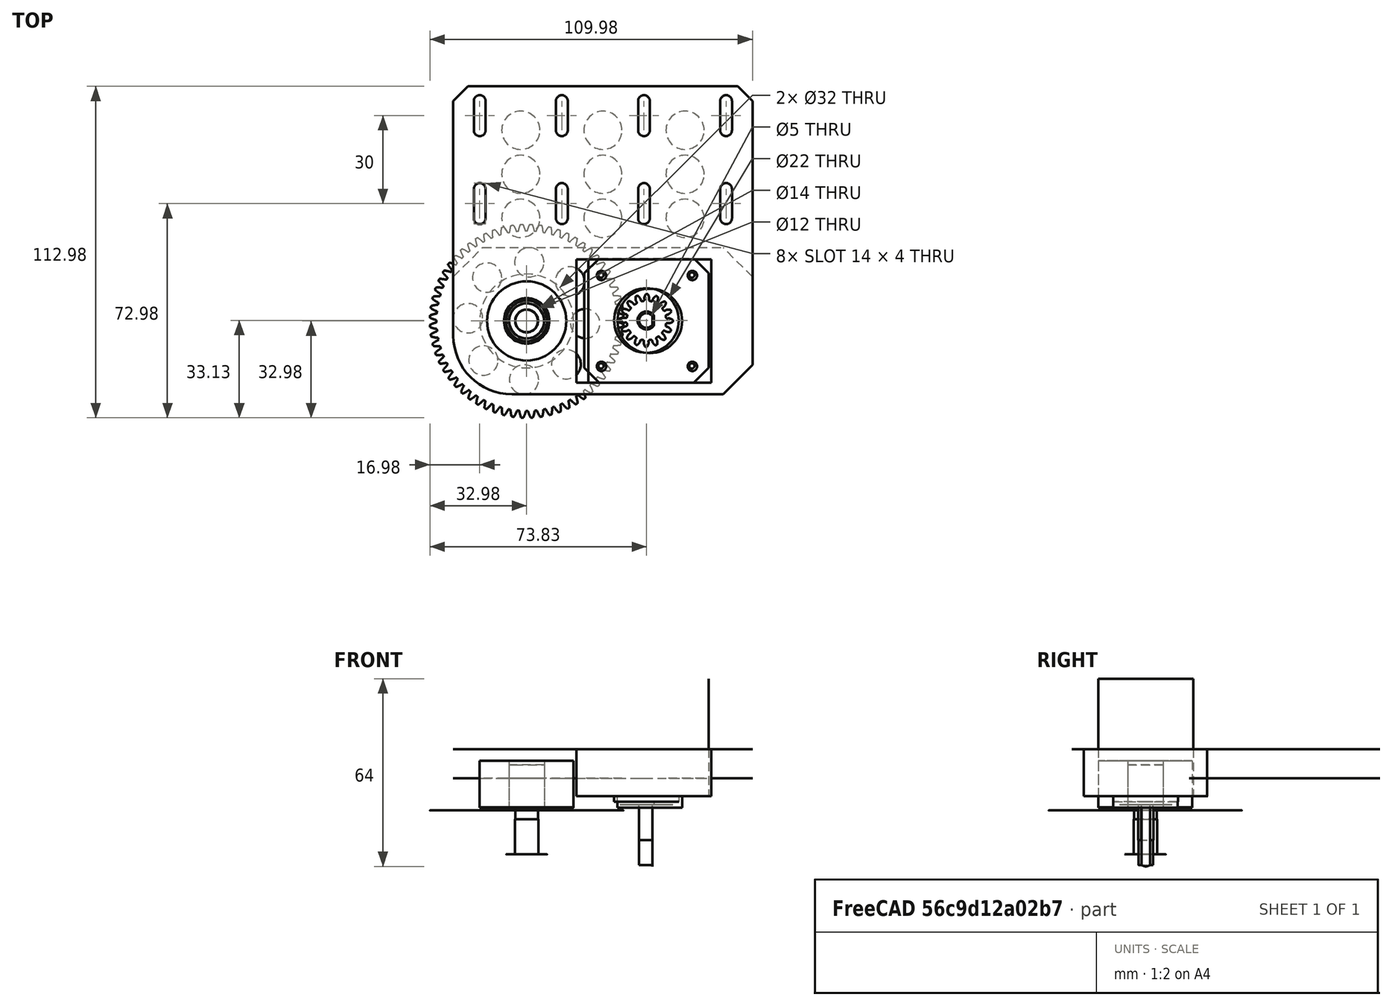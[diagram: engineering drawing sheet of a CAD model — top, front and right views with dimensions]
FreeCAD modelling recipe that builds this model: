
FCSTD DOCUMENT  (FreeCAD 2020.12.13R23076 +3015 (Git))
Label: przekladnia
License: All rights reserved
LicenseURL: http://en.wikipedia.org/wiki/All_rights_reserved
objects: Part::FeaturePython×44, App::FeaturePython×43, App::Link×7
note: 43 computed .brp shape members not serialized (recipe doc carries the construction recipe); baked Part::Feature solids carry a one-line shape summary decoded from their .brp
EXTERNAL_REF file=plytaprzekladni.FCStd obj=Body
EXTERNAL_REF file=krokowiec-nema17.FCStd obj=Body
EXTERNAL_REF file=kolkozebmodul1fi5przekl.FCStd obj=Body
EXTERNAL_REF file=lozysko 5201.FCStd obj=Body
EXTERNAL_REF file=koloprzekladni.FCStd obj=Body
EXTERNAL_REF file=m8x40imb.FCStd obj=Body
EXTERNAL_REF file=wkladkaloz.FCStd obj=Body

FEATURE [App::Link] Link001  label="plyta-przekadni"
  LinkPlacement = pos=(0,0,0) rot=(-1,0,0;3.14159rad)
  LinkedObject = -> <external plytaprzekladni.FCStd>#Body
  Placement = pos=(0,0,0) rot=(-1,0,0;3.14159rad)
  SyncGroupVisibility = false
  _LinkVersion = 1
FEATURE [App::Link] Link003  label="nema17"
  LinkPlacement = pos=(0.85,0.15,24) rot=(1,0,0;3.14159rad)
  LinkedObject = -> <external krokowiec-nema17.FCStd>#Body
  Placement = pos=(0.85,0.15,24) rot=(1,0,0;3.14159rad)
  SyncGroupVisibility = false
  _LinkVersion = 1
FEATURE [App::Link] Link  label="kolkozebstozniskie"
  LinkPlacement = pos=(0.85,0.15,-31) rot=(0,0,-1;0.012799rad)
  LinkedObject = -> <external kolkozebmodul1fi5przekl.FCStd>#Body
  Placement = pos=(0.85,0.15,-31) rot=(0,0,-1;0.012799rad)
  SyncGroupVisibility = false
  _LinkVersion = 1
FEATURE [App::Link] Link004  label="lozysko5201"
  LinkPlacement = pos=(-40,1.5e-15,-11.95) rot=(0,0,-1;0.034901rad)
  LinkedObject = -> <external lozysko 5201.FCStd>#Body
  Placement = pos=(-40,1.5e-15,-11.95) rot=(0,0,-1;0.034901rad)
  SyncGroupVisibility = false
  _LinkVersion = 1
FEATURE [App::Link] Link006  label="koloprzekladni"
  LinkPlacement = pos=(-40,3.8e-15,-30.9) rot=(-0.999741,0.022763,0;3.14159rad)
  LinkedObject = -> <external koloprzekladni.FCStd>#Body
  Placement = pos=(-40,3.8e-15,-30.9) rot=(-0.999741,0.022763,0;3.14159rad)
  SyncGroupVisibility = false
  _LinkVersion = 1
FEATURE [App::Link] Link007  label="m8x40imb"
  LinkPlacement = pos=(-40,5.4e-15,-43.9) rot=(0,0,-1;0.002436rad)
  LinkedObject = -> <external m8x40imb.FCStd>#Body
  Placement = pos=(-40,5.4e-15,-43.9) rot=(0,0,-1;0.002436rad)
  SyncGroupVisibility = false
  _LinkVersion = 1
FEATURE [App::Link] Link005  label="wkladkamimosr"
  LinkPlacement = pos=(-40,2.5e-15,-20.9) rot=(0,0,1;3.95082rad)
  LinkedObject = -> <external wkladkaloz.FCStd>#Body
  Placement = pos=(-40,2.5e-15,-20.9) rot=(0,0,1;3.95082rad)
  SyncGroupVisibility = false
  _LinkVersion = 1
FEATURE [Part::FeaturePython] Parts  # WARN: FeaturePython — macro-defined, semantics opaque (R4)
  Group = -> [Link001,Link003,Link,Link004,Link006,Link007,Link005]
  GroupMode = 0
  _LinkVersion = 1
FEATURE [Part::FeaturePython] Assembly  label="przekladnia"  # WARN: FeaturePython — macro-defined, semantics opaque (R4)
  AutoRelax = true
  BuildShape = 0
  Freeze = false
  Group = -> [Constraints,Elements,Parts]
  Verbose = false
  _LinkVersion = 1
  _SolverType = 1
  _Version = 1
FEATURE [App::FeaturePython] Constraints  # WARN: FeaturePython — macro-defined, semantics opaque (R4)
  Group = -> [Constraint,Constraint002,Constraint005,Constraint015,Constraint016,Constraint020,Constraint021,Constraint022,Constraint023,Constraint024,Constraint025,Constraint026,Constraint027,Constraint028]
  _LinkVersion = 1
  _Version = 1
FEATURE [App::FeaturePython] Elements  # WARN: FeaturePython — macro-defined, semantics opaque (R4)
  Group = -> [_Element,_Element001,_Element002,_Element003,_Element004,_Element006,_Element007,_Element009,_Element010,_Element011,_Element012,_Element014,_Element016,_Element017,_Element019,_Element022,_Element023,_Element024,_Element025,_Element028,Element,Element001,_Element029,_Element030,_Element031,_Element032,_Element033,_Element034,_Element035,_Element036,_Element037,_Element038,_Element039,_Element040,+8 more]
  _LinkVersion = 1
FEATURE [App::FeaturePython] Constraint  label="Locked"  # WARN: FeaturePython — macro-defined, semantics opaque (R4)
  Disabled = false
  Group = -> [ElementLink]
  _ConstraintType = 0
  _LinkVersion = 1
  _Parent = -> Constraints
FEATURE [App::FeaturePython] ElementLink  label="_Element"  # link proxy (typed FeaturePython)
  LinkTransform = true
  LinkedObject = -> _Element
  _LinkVersion = 1
  _Parent = -> Constraint
FEATURE [Part::FeaturePython] _Element  # link proxy (typed FeaturePython)
  Detach = false
  LinkTransform = true
  LinkedObject = -> Link001 [Pocket005.Face1]
  _LinkVersion = 1
  _Parent = -> Elements
FEATURE [Part::FeaturePython] _Element001  # link proxy (typed FeaturePython)
  Detach = false
  LinkTransform = true
  LinkedObject = -> Link001 [Pocket005.Face57]
  _LinkVersion = 1
  _Parent = -> Elements
FEATURE [Part::FeaturePython] _Element002  # link proxy (typed FeaturePython)
  Detach = false
  LinkTransform = true
  LinkedObject = -> Link003 [Chamfer001.Face13]
  _LinkVersion = 1
  _Parent = -> Elements
FEATURE [Part::FeaturePython] _Element003  # link proxy (typed FeaturePython)
  Detach = false
  LinkTransform = true
  LinkedObject = -> Link003 [Chamfer001.Face1]
  _LinkVersion = 1
  _Parent = -> Elements
FEATURE [Part::FeaturePython] _Element004  # link proxy (typed FeaturePython)
  Detach = false
  LinkTransform = true
  LinkedObject = -> Link001 [Pocket005.Face52]
  _LinkVersion = 1
  _Parent = -> Elements
FEATURE [Part::FeaturePython] _Element006  # link proxy (typed FeaturePython)
  Detach = false
  LinkTransform = true
  LinkedObject = -> Link003 [Chamfer001.Face21]
  _LinkVersion = 1
  _Parent = -> Elements
FEATURE [Part::FeaturePython] _Element007  # link proxy (typed FeaturePython)
  Detach = false
  LinkTransform = true
  LinkedObject = -> Link003 [Chamfer001.Face22]
  _LinkVersion = 1
  _Parent = -> Elements
FEATURE [App::FeaturePython] Constraint005  label="AxialAlignment002"  # WARN: FeaturePython — macro-defined, semantics opaque (R4)
  Angle = 0
  AnglePitch = 0
  AngleRoll = 0
  Disabled = false
  Group = -> [ElementLink009,ElementLink010]
  LockAngle = false
  Multiply = false
  _ConstraintType = 36
  _LinkVersion = 1
  _Parent = -> Constraints
FEATURE [App::FeaturePython] ElementLink009  label="_Element009"  # link proxy (typed FeaturePython)
  LinkTransform = true
  LinkedObject = -> _Element009
  _LinkVersion = 1
  _Parent = -> Constraint005
FEATURE [Part::FeaturePython] _Element009  # link proxy (typed FeaturePython)
  Detach = false
  LinkTransform = true
  LinkedObject = -> Link001 [Pocket005.Face54]
  _LinkVersion = 1
  _Parent = -> Elements
FEATURE [App::FeaturePython] ElementLink010  label="_Element010"  # link proxy (typed FeaturePython)
  LinkTransform = true
  LinkedObject = -> _Element010
  _LinkVersion = 1
  _Parent = -> Constraint005
FEATURE [Part::FeaturePython] _Element010  # link proxy (typed FeaturePython)
  Detach = false
  LinkTransform = true
  LinkedObject = -> Link004 [Mirrored.Face1]
  _LinkVersion = 1
  _Parent = -> Elements
FEATURE [Part::FeaturePython] _Element011  # link proxy (typed FeaturePython)
  Detach = false
  LinkTransform = true
  LinkedObject = -> Link004 [Mirrored.Face3]
  _LinkVersion = 1
  _Parent = -> Elements
FEATURE [Part::FeaturePython] _Element012  # link proxy (typed FeaturePython)
  Detach = false
  LinkTransform = true
  LinkedObject = -> Link001 [Pocket005.Face51]
  _LinkVersion = 1
  _Parent = -> Elements
FEATURE [Part::FeaturePython] _Element014  # link proxy (typed FeaturePython)
  Detach = false
  LinkTransform = true
  LinkedObject = -> Link004 [Mirrored.Face12]
  _LinkVersion = 1
  _Parent = -> Elements
FEATURE [Part::FeaturePython] _Element016  # link proxy (typed FeaturePython)
  Detach = false
  LinkTransform = true
  LinkedObject = -> Link004 [Mirrored.Face10]
  _LinkVersion = 1
  _Parent = -> Elements
FEATURE [Part::FeaturePython] _Element017  # link proxy (typed FeaturePython)
  Detach = false
  LinkTransform = true
  LinkedObject = -> Link006 [Groove.Face259]
  _LinkVersion = 1
  _Parent = -> Elements
FEATURE [Part::FeaturePython] _Element019  # link proxy (typed FeaturePython)
  Detach = false
  LinkTransform = true
  LinkedObject = -> Link006 [Groove.Edge264]
  _LinkVersion = 1
  _Parent = -> Elements
FEATURE [Part::FeaturePython] _Element022  # link proxy (typed FeaturePython)
  Detach = false
  LinkTransform = true
  LinkedObject = -> Link006 [Groove.Face4]
  _LinkVersion = 1
  _Parent = -> Elements
FEATURE [Part::FeaturePython] _Element023  # link proxy (typed FeaturePython)
  Detach = false
  LinkTransform = true
  LinkedObject = -> Link007 [BaseFeature.Face4]
  _LinkVersion = 1
  _Parent = -> Elements
FEATURE [Part::FeaturePython] _Element024  # link proxy (typed FeaturePython)
  Detach = false
  LinkTransform = true
  LinkedObject = -> Link007 [BaseFeature.Face2]
  _LinkVersion = 1
  _Parent = -> Elements
FEATURE [Part::FeaturePython] _Element025  # link proxy (typed FeaturePython)
  Detach = false
  LinkTransform = true
  LinkedObject = -> Link006 [Groove.Face380]
  _LinkVersion = 1
  _Parent = -> Elements
FEATURE [Part::FeaturePython] _Element028  # link proxy (typed FeaturePython)
  Detach = false
  LinkTransform = true
  LinkedObject = -> Link003 [Chamfer001.Face23]
  _LinkVersion = 1
  _Parent = -> Elements
FEATURE [Part::FeaturePython] Element  # link proxy (typed FeaturePython)
  Detach = false
  LinkTransform = true
  LinkedObject = -> Link001 [MultiTransform001.Face47]
  _LinkVersion = 1
  _Parent = -> Elements
FEATURE [Part::FeaturePython] Element001  # link proxy (typed FeaturePython)
  Detach = false
  LinkTransform = true
  LinkedObject = -> Link001 [MultiTransform001.Face1]
  _LinkVersion = 1
  _Parent = -> Elements
FEATURE [App::FeaturePython] ElementLink003  label="_Element003"  # link proxy (typed FeaturePython)
  LinkTransform = true
  LinkedObject = -> _Element003
  _LinkVersion = 1
  _Parent = -> Constraint002
FEATURE [App::FeaturePython] ElementLink004  label="_Element004"  # link proxy (typed FeaturePython)
  LinkTransform = true
  LinkedObject = -> _Element004
  _LinkVersion = 1
  _Parent = -> Constraint002
FEATURE [App::FeaturePython] Constraint002  label="PlaneAlignment"  # WARN: FeaturePython — macro-defined, semantics opaque (R4)
  Angle = 0
  AnglePitch = 0
  AngleRoll = 0
  Cascade = false
  Disabled = false
  Group = -> [ElementLink003,ElementLink004]
  LockAngle = false
  _ConstraintType = 37
  _LinkVersion = 1
  _Parent = -> Constraints
FEATURE [App::FeaturePython] Constraint015  label="MultiParallel"  # WARN: FeaturePython — macro-defined, semantics opaque (R4)
  Angle = 0
  AnglePitch = 0
  AngleRoll = 0
  Disabled = false
  Group = -> [ElementLink029,ElementLink030]
  LockAngle = false
  _ConstraintType = 291
  _LinkVersion = 1
  _Parent = -> Constraints
FEATURE [App::FeaturePython] ElementLink029  label="_Element029"  # link proxy (typed FeaturePython)
  LinkTransform = true
  LinkedObject = -> _Element029
  _LinkVersion = 1
  _Parent = -> Constraint015
FEATURE [Part::FeaturePython] _Element029  # link proxy (typed FeaturePython)
  Detach = false
  LinkTransform = true
  LinkedObject = -> Link003 [Chamfer001.Face5]
  _LinkVersion = 1
  _Parent = -> Elements
FEATURE [App::FeaturePython] ElementLink030  label="_Element030"  # link proxy (typed FeaturePython)
  LinkTransform = true
  LinkedObject = -> _Element030
  _LinkVersion = 1
  _Parent = -> Constraint015
FEATURE [Part::FeaturePython] _Element030  # link proxy (typed FeaturePython)
  Detach = false
  LinkTransform = true
  LinkedObject = -> Link001 [MultiTransform001.Face44]
  _LinkVersion = 1
  _Parent = -> Elements
FEATURE [App::FeaturePython] Constraint016  label="PointsPlaneDistance"  # WARN: FeaturePython — macro-defined, semantics opaque (R4)
  Disabled = false
  Distance = -1
  Group = -> [ElementLink031,ElementLink032]
  _ConstraintType = 7
  _LinkVersion = 1
  _Parent = -> Constraints
FEATURE [App::FeaturePython] ElementLink031  label="_Element031"  # link proxy (typed FeaturePython)
  LinkTransform = true
  LinkedObject = -> _Element031
  _LinkVersion = 1
  _Parent = -> Constraint016
FEATURE [Part::FeaturePython] _Element031  # link proxy (typed FeaturePython)
  Detach = false
  LinkTransform = true
  LinkedObject = -> Link003 [Chamfer001.Vertex3]
  _LinkVersion = 1
  _Parent = -> Elements
FEATURE [App::FeaturePython] ElementLink032  label="_Element030"  # link proxy (typed FeaturePython)
  LinkTransform = true
  LinkedObject = -> _Element030
  _LinkVersion = 1
  _Parent = -> Constraint016
FEATURE [Part::FeaturePython] _Element032  # link proxy (typed FeaturePython)
  Detach = false
  LinkTransform = true
  LinkedObject = -> Link [Chamfer.Vertex2]
  _LinkVersion = 1
  _Parent = -> Elements
FEATURE [App::FeaturePython] Constraint020  label="AxialAlignment"  # WARN: FeaturePython — macro-defined, semantics opaque (R4)
  Angle = 0
  AnglePitch = 0
  AngleRoll = 0
  Disabled = false
  Group = -> [ElementLink039,ElementLink040]
  LockAngle = false
  Multiply = false
  _ConstraintType = 36
  _LinkVersion = 0
  _Parent = -> Constraints
FEATURE [App::FeaturePython] ElementLink039  label="_Element010"  # link proxy (typed FeaturePython)
  LinkTransform = true
  LinkedObject = -> _Element010
  _LinkVersion = 0
  _Parent = -> Constraint020
FEATURE [App::FeaturePython] ElementLink040  label="_Element033"  # link proxy (typed FeaturePython)
  LinkTransform = true
  LinkedObject = -> _Element033
  _LinkVersion = 0
  _Parent = -> Constraint020
FEATURE [Part::FeaturePython] _Element033  # link proxy (typed FeaturePython)
  Detach = false
  LinkTransform = true
  LinkedObject = -> Link001 [MultiTransform001.Face51]
  _LinkVersion = 0
  _Parent = -> Elements
FEATURE [Part::FeaturePython] _Element034  # link proxy (typed FeaturePython)
  Detach = false
  LinkTransform = true
  LinkedObject = -> Link004 [Mirrored.Vertex2]
  _LinkVersion = 0
  _Parent = -> Elements
FEATURE [Part::FeaturePython] _Element035  # link proxy (typed FeaturePython)
  Detach = false
  LinkTransform = true
  LinkedObject = -> Link001 [MultiTransform001.Face49]
  _LinkVersion = 0
  _Parent = -> Elements
FEATURE [App::FeaturePython] Constraint021  label="PointInPlane001"  # WARN: FeaturePython — macro-defined, semantics opaque (R4)
  Disabled = false
  Group = -> [ElementLink041,ElementLink042]
  _ConstraintType = 3
  _LinkVersion = 0
  _Parent = -> Constraints
FEATURE [App::FeaturePython] ElementLink041  label="_Element034"  # link proxy (typed FeaturePython)
  LinkTransform = true
  LinkedObject = -> _Element034
  _LinkVersion = 0
  _Parent = -> Constraint021
FEATURE [App::FeaturePython] ElementLink042  label="_Element035"  # link proxy (typed FeaturePython)
  LinkTransform = true
  LinkedObject = -> _Element035
  _LinkVersion = 0
  _Parent = -> Constraint021
FEATURE [App::FeaturePython] Constraint022  label="AxialAlignment003"  # WARN: FeaturePython — macro-defined, semantics opaque (R4)
  Angle = 0
  AnglePitch = 0
  AngleRoll = 0
  Disabled = false
  Group = -> [ElementLink043,ElementLink044]
  LockAngle = false
  Multiply = false
  _ConstraintType = 36
  _LinkVersion = 0
  _Parent = -> Constraints
FEATURE [App::FeaturePython] ElementLink043  label="_Element036"  # link proxy (typed FeaturePython)
  LinkTransform = true
  LinkedObject = -> _Element036
  _LinkVersion = 0
  _Parent = -> Constraint022
FEATURE [Part::FeaturePython] _Element036  # link proxy (typed FeaturePython)
  Detach = false
  LinkTransform = true
  LinkedObject = -> Link005 [Pocket.Face1]
  _LinkVersion = 0
  _Parent = -> Elements
FEATURE [App::FeaturePython] ElementLink044  label="_Element014"  # link proxy (typed FeaturePython)
  LinkTransform = true
  LinkedObject = -> _Element014
  _LinkVersion = 0
  _Parent = -> Constraint022
FEATURE [App::FeaturePython] Constraint023  label="PointInPlane002"  # WARN: FeaturePython — macro-defined, semantics opaque (R4)
  Disabled = false
  Group = -> [ElementLink045,ElementLink046]
  _ConstraintType = 3
  _LinkVersion = 0
  _Parent = -> Constraints
FEATURE [App::FeaturePython] ElementLink045  label="_Element037"  # link proxy (typed FeaturePython)
  LinkTransform = true
  LinkedObject = -> _Element037
  _LinkVersion = 0
  _Parent = -> Constraint023
FEATURE [Part::FeaturePython] _Element037  # link proxy (typed FeaturePython)
  Detach = false
  LinkTransform = true
  LinkedObject = -> Link005 [Pocket.Vertex4]
  _LinkVersion = 0
  _Parent = -> Elements
FEATURE [App::FeaturePython] ElementLink046  label="_Element016"  # link proxy (typed FeaturePython)
  LinkTransform = true
  LinkedObject = -> _Element016
  _LinkVersion = 0
  _Parent = -> Constraint023
FEATURE [App::FeaturePython] Constraint024  label="AxialAlignment004"  # WARN: FeaturePython — macro-defined, semantics opaque (R4)
  Angle = 0
  AnglePitch = 0
  AngleRoll = 0
  Disabled = false
  Group = -> [ElementLink047,ElementLink048]
  LockAngle = false
  Multiply = false
  _ConstraintType = 36
  _LinkVersion = 0
  _Parent = -> Constraints
FEATURE [App::FeaturePython] ElementLink047  label="_Element038"  # link proxy (typed FeaturePython)
  LinkTransform = true
  LinkedObject = -> _Element038
  _LinkVersion = 0
  _Parent = -> Constraint024
FEATURE [Part::FeaturePython] _Element038  # link proxy (typed FeaturePython)
  Detach = false
  LinkTransform = true
  LinkedObject = -> Link005 [Pocket.Face5]
  _LinkVersion = 0
  _Parent = -> Elements
FEATURE [App::FeaturePython] ElementLink048  label="_Element039"  # link proxy (typed FeaturePython)
  LinkTransform = true
  LinkedObject = -> _Element039
  _LinkVersion = 0
  _Parent = -> Constraint024
FEATURE [Part::FeaturePython] _Element039  # link proxy (typed FeaturePython)
  Detach = false
  LinkTransform = true
  LinkedObject = -> Link006 [PolarPattern.Face262]
  _LinkVersion = 0
  _Parent = -> Elements
FEATURE [Part::FeaturePython] _Element040  # link proxy (typed FeaturePython)
  Detach = false
  LinkTransform = true
  LinkedObject = -> Link006 [PolarPattern.Vertex264]
  _LinkVersion = 0
  _Parent = -> Elements
FEATURE [Part::FeaturePython] _Element041  # link proxy (typed FeaturePython)
  Detach = false
  LinkTransform = true
  LinkedObject = -> Link005 [Pocket.Face7]
  _LinkVersion = 0
  _Parent = -> Elements
FEATURE [App::FeaturePython] Constraint025  label="PointInPlane003"  # WARN: FeaturePython — macro-defined, semantics opaque (R4)
  Disabled = false
  Group = -> [ElementLink049,ElementLink050]
  _ConstraintType = 3
  _LinkVersion = 0
  _Parent = -> Constraints
FEATURE [App::FeaturePython] ElementLink049  label="_Element042"  # link proxy (typed FeaturePython)
  LinkTransform = true
  LinkedObject = -> _Element042
  _LinkVersion = 0
  _Parent = -> Constraint025
FEATURE [Part::FeaturePython] _Element042  # link proxy (typed FeaturePython)
  Detach = false
  LinkTransform = true
  LinkedObject = -> Link005 [Pocket.Vertex6]
  _LinkVersion = 0
  _Parent = -> Elements
FEATURE [App::FeaturePython] ElementLink050  label="_Element043"  # link proxy (typed FeaturePython)
  LinkTransform = true
  LinkedObject = -> _Element043
  _LinkVersion = 0
  _Parent = -> Constraint025
FEATURE [Part::FeaturePython] _Element043  # link proxy (typed FeaturePython)
  Detach = false
  LinkTransform = true
  LinkedObject = -> Link006 [PolarPattern.Face4]
  _LinkVersion = 0
  _Parent = -> Elements
FEATURE [App::FeaturePython] Constraint026  label="AxialAlignment005"  # WARN: FeaturePython — macro-defined, semantics opaque (R4)
  Angle = 0
  AnglePitch = 0
  AngleRoll = 0
  Disabled = false
  Group = -> [ElementLink051,ElementLink052]
  LockAngle = false
  Multiply = false
  _ConstraintType = 36
  _LinkVersion = 0
  _Parent = -> Constraints
FEATURE [App::FeaturePython] ElementLink051  label="_Element044"  # link proxy (typed FeaturePython)
  LinkTransform = true
  LinkedObject = -> _Element044
  _LinkVersion = 0
  _Parent = -> Constraint026
FEATURE [Part::FeaturePython] _Element044  # link proxy (typed FeaturePython)
  Detach = false
  LinkTransform = true
  LinkedObject = -> Link [Chamfer.Face101]
  _LinkVersion = 0
  _Parent = -> Elements
FEATURE [App::FeaturePython] ElementLink052  label="_Element006"  # link proxy (typed FeaturePython)
  LinkTransform = true
  LinkedObject = -> _Element006
  _LinkVersion = 0
  _Parent = -> Constraint026
FEATURE [App::FeaturePython] Constraint027  label="PointInPlane"  # WARN: FeaturePython — macro-defined, semantics opaque (R4)
  Disabled = false
  Group = -> [ElementLink053,ElementLink054]
  _ConstraintType = 3
  _LinkVersion = 0
  _Parent = -> Constraints
FEATURE [App::FeaturePython] ElementLink053  label="_Element045"  # link proxy (typed FeaturePython)
  LinkTransform = true
  LinkedObject = -> _Element045
  _LinkVersion = 0
  _Parent = -> Constraint027
FEATURE [Part::FeaturePython] _Element045  # link proxy (typed FeaturePython)
  Detach = false
  LinkTransform = true
  LinkedObject = -> Link003 [Chamfer001.Vertex32]
  _LinkVersion = 0
  _Parent = -> Elements
FEATURE [App::FeaturePython] ElementLink054  label="_Element046"  # link proxy (typed FeaturePython)
  LinkTransform = true
  LinkedObject = -> _Element046
  _LinkVersion = 0
  _Parent = -> Constraint027
FEATURE [Part::FeaturePython] _Element046  # link proxy (typed FeaturePython)
  Detach = false
  LinkTransform = true
  LinkedObject = -> Link [Chamfer.Face1]
  _LinkVersion = 0
  _Parent = -> Elements
FEATURE [App::FeaturePython] Constraint028  label="PointInPlane004"  # WARN: FeaturePython — macro-defined, semantics opaque (R4)
  Disabled = false
  Group = -> [ElementLink055,ElementLink056]
  _ConstraintType = 3
  _LinkVersion = 0
  _Parent = -> Constraints
FEATURE [App::FeaturePython] ElementLink055  label="_Element047"  # link proxy (typed FeaturePython)
  LinkTransform = true
  LinkedObject = -> _Element047
  _LinkVersion = 0
  _Parent = -> Constraint028
FEATURE [Part::FeaturePython] _Element047  # link proxy (typed FeaturePython)
  Detach = false
  LinkTransform = true
  LinkedObject = -> Link003 [Chamfer001.Vertex15]
  _LinkVersion = 0
  _Parent = -> Elements
FEATURE [App::FeaturePython] ElementLink056  label="_Element048"  # link proxy (typed FeaturePython)
  LinkTransform = true
  LinkedObject = -> _Element048
  _LinkVersion = 0
  _Parent = -> Constraint028
FEATURE [Part::FeaturePython] _Element048  # link proxy (typed FeaturePython)
  Detach = false
  LinkTransform = true
  LinkedObject = -> Link001 [MultiTransform001.Face87]
  _LinkVersion = 0
  _Parent = -> Elements

RESOLVED EXTERNAL PARTS (link-assembly join: the EXTERNAL_REF files above that resolve inside this repo's crawl, each included once):
---- part kolkozebmodul1fi5przekl.FCStd = doc fcstd_9557186af2d1 ----
FCSTD DOCUMENT  (FreeCAD 2020.12.13R23076 +3015 (Git))
Label: kolkozebmodul1fi5przekl
License: All rights reserved
objects: Part::FeaturePython×1, PartDesign::FeatureBase×1, Sketcher::SketchObject×1, PartDesign::Pocket×1, PartDesign::Chamfer×1, PartDesign::Body×1
note: 11 computed .brp shape members not serialized (recipe doc carries the construction recipe); baked Part::Feature solids carry a one-line shape summary decoded from their .brp

FEATURE [Part::FeaturePython] involutegear  # WARN: FeaturePython — macro-defined, semantics opaque (R4)
  backlash = 0
  beta = 0
  clearance = 0.25
  double_helix = false
  dw = 16
  head = 0
  height = 12
  module = 1
  numpoints = 6
  pressure_angle = 20
  properties_from_tool = true
  reversed_backlash = false
  shift = 0
  simple = false
  teeth = 16
  transverse_pitch = 3.14159
  undercut = true
FEATURE [PartDesign::FeatureBase] BaseFeature
  BaseFeature = -> involutegear
  NewSolid = false
  Suppress = false
FEATURE [Sketcher::SketchObject] Sketch
  MapMode = 5
  Placement = pos=(0,0,0) rot=(1,0,0;3.14159rad)
  Support = -> [BaseFeature]
  sketch-geometry (2):
    g0: ArcOfCircle CenterX=0 CenterY=0 CenterZ=0 NormalX=0 NormalY=0 NormalZ=1 AngleXU=0 Radius=2.55 StartAngle=0.636936 EndAngle=5.64625
    g1: LineSegment StartX=2.05 StartY=1.51658 StartZ=0 EndX=2.05 EndY=-1.51658 EndZ=0
  constraints (6):
    c: Coincident(g0,g-1)
    c: Diameter(g0) = 5.1
    c: Vertical(g1)
    c: Coincident(g0,g1)
    c: Coincident(g0,g1)
    c: DistanceX(g0) = 2.05
FEATURE [PartDesign::Pocket] Pocket
  BaseFeature = -> BaseFeature
  ClaimChildren = false
  Fit = 0
  FitJoin = 0
  InnerFit = 0
  InnerFitJoin = 0
  InnerTaperAngle = 0
  InnerTaperAngleRev = 0
  Length = 25
  Length2 = 100
  NewSolid = false
  Profile = -> Sketch
  Suppress = false
  Type = 1
FEATURE [PartDesign::Chamfer] Chamfer
  Angle = 45
  Base = -> Pocket [Edge199,Edge200]
  BaseFeature = -> Pocket
  ChamferType = 1
  FlipDirection = false
  NewSolid = false
  Size = 0.5
  Size2 = 1
  SupportTransform = true
  Suppress = false
FEATURE [PartDesign::Body] Body  label="kolkozebstozniskie"
  BaseFeature = -> involutegear
  ExportMode = 0
  Group = -> [BaseFeature,Sketch,Pocket,Chamfer]
  Origin = -> Origin
  Tip = -> Chamfer
  _ExportChildren = -> [BaseFeature,Pocket,Chamfer]
  _GroupVersion = 1
---- part koloprzekladni.FCStd = doc fcstd_f7d769585b6c ----
FCSTD DOCUMENT  (FreeCAD 2020.10.16R22739 +2665 (Git))
Label: koloprzekladni
License: All rights reserved
LicenseURL: http://en.wikipedia.org/wiki/All_rights_reserved
objects: Sketcher::SketchObject×3, Part::FeaturePython×2, PartDesign::Groove×2, Part::Fuse×1, PartDesign::FeatureBase×1, PartDesign::Pocket×1, PartDesign::PolarPattern×1, PartDesign::Body×1
note: 20 computed .brp shape members not serialized (recipe doc carries the construction recipe); baked Part::Feature solids carry a one-line shape summary decoded from their .brp

FEATURE [Part::FeaturePython] involutegear  # WARN: FeaturePython — macro-defined, semantics opaque (R4)
  backlash = 0
  beta = 0
  clearance = 0.25
  double_helix = false
  dw = 20
  head = 0
  height = 15
  module = 1
  numpoints = 6
  pressure_angle = 20
  properties_from_tool = true
  reversed_backlash = false
  shift = 0
  simple = false
  teeth = 20
  transverse_pitch = 3.14159
  undercut = false
FEATURE [Part::FeaturePython] involutegear001  # WARN: FeaturePython — macro-defined, semantics opaque (R4)
  Placement = pos=(0,0,-10) rot=(0,0,1;0rad)
  backlash = 0
  beta = 0
  clearance = 0.25
  double_helix = false
  dw = 64
  head = 0
  height = 10
  module = 1
  numpoints = 6
  pressure_angle = 20
  properties_from_tool = true
  reversed_backlash = false
  shift = 0
  simple = false
  teeth = 64
  transverse_pitch = 3.14159
  undercut = false
FEATURE [Sketcher::SketchObject] Sketch
  MapMode = 5
  Placement = pos=(0,0,0) rot=(0.57735,0.57735,0.57735;2.0944rad)
  Support = -> [YZ_Plane]
  sketch-geometry (6):
    g0: LineSegment StartX=0 StartY=20 StartZ=0 EndX=7 EndY=20 EndZ=0
    g1: LineSegment StartX=7 StartY=20 StartZ=0 EndX=7 EndY=5 EndZ=0
    g2: LineSegment StartX=7 StartY=5 StartZ=0 EndX=3.9 EndY=5 EndZ=0
    g3: LineSegment StartX=3.9 StartY=5 StartZ=0 EndX=3.9 EndY=-20 EndZ=0
    g4: LineSegment StartX=3.9 StartY=-20 StartZ=0 EndX=0 EndY=-20 EndZ=0
    g5: LineSegment StartX=0 StartY=-20 StartZ=0 EndX=0 EndY=20 EndZ=0
  constraints (18):
    c: PointOnObject(g0,g-2)
    c: Horizontal(g0)
    c: Coincident(g0,g1)
    c: Vertical(g1)
    c: Coincident(g1,g2)
    c: Horizontal(g2)
    c: Coincident(g2,g3)
    c: Vertical(g3)
    c: Coincident(g3,g4)
    c: PointOnObject(g4,g-2)
    c: Horizontal(g4)
    c: Coincident(g4,g5)
    c: Coincident(g5,g0)
    c: DistanceX(g0) = 7
    c: DistanceY(g0) = 20
    c: DistanceX(g2) = 3.9
    c: DistanceY(g4) = -20
    c: DistanceY(g1) = 5
FEATURE [Part::Fuse] Fusion
  Base = -> involutegear
  Tool = -> involutegear001
FEATURE [PartDesign::FeatureBase] BaseFeature
  BaseFeature = -> Fusion
  NewSolid = false
  Suppress = false
FEATURE [PartDesign::Groove] Groove
  Angle = 360
  Axis = (-2e-16,3e-16,1)
  Base = (0,0,0)
  BaseFeature = -> BaseFeature
  ClaimChildren = false
  NewSolid = false
  Profile = -> Sketch
  ReferenceAxis = -> Sketch [V_Axis]
  Suppress = false
FEATURE [Sketcher::SketchObject] Sketch001
  MapMode = 5
  Placement = pos=(0,0,0) rot=(1,0,0;1.5708rad)
  Support = -> [XZ_Plane]
  sketch-geometry (4):
    g0: LineSegment StartX=-28 StartY=0 StartZ=0 EndX=-25.8162 EndY=-6 EndZ=0
    g1: LineSegment StartX=-25.8162 StartY=-6 StartZ=0 EndX=-14.1838 EndY=-6 EndZ=0
    g2: LineSegment StartX=-14.1838 StartY=-6 StartZ=0 EndX=-12 EndY=0 EndZ=0
    g3: LineSegment StartX=-12 StartY=0 StartZ=0 EndX=-28 EndY=0 EndZ=0
  constraints (12):
    c: Coincident(g0,g1)
    c: Horizontal(g1)
    c: Coincident(g1,g2)
    c: Coincident(g2,g3)
    c: Coincident(g3,g0)
    c: Horizontal(g3)
    c: DistanceY(g1) = -6
    c: DistanceX(g0) = -28
    c: DistanceX(g2) = -12
    c: DistanceY(g2) = 0
    c: Equal(g2,g0)
    c: Angle(g2,g1) = 1.91986
FEATURE [PartDesign::Groove] Groove001
  Angle = 360
  Axis = (0,-2e-16,1)
  Base = (0,0,0)
  BaseFeature = -> Groove
  ClaimChildren = false
  NewSolid = false
  Profile = -> Sketch001
  ReferenceAxis = -> Sketch001 [V_Axis]
  Reversed = true
  Suppress = false
FEATURE [Sketcher::SketchObject] Sketch002
  MapMode = 5
  Support = -> [XY_Plane]
  sketch-geometry (1):
    g0: Circle CenterX=0 CenterY=20 CenterZ=0 NormalX=0 NormalY=0 NormalZ=1 AngleXU=0 Radius=5
  constraints (3):
    c: PointOnObject(g0,g-2)
    c: Diameter(g0) = 10
    c: DistanceY(g0) = 20
FEATURE [PartDesign::Pocket] Pocket
  BaseFeature = -> Groove001
  ClaimChildren = false
  Length = 5
  Length2 = 100
  NewSolid = false
  Profile = -> Sketch002
  Suppress = false
  Type = 1
FEATURE [PartDesign::PolarPattern] PolarPattern
  Angle = 360
  Axis = -> Sketch002 [N_Axis]
  BaseFeature = -> Pocket
  CopyShape = false
  NewSolid = false
  Occurrences = 8
  OriginalSubs = -> [Pocket]
  Originals = -> [Pocket]
  SubTransform = true
  Suppress = false
FEATURE [PartDesign::Body] Body  label="koloprzekladni"
  BaseFeature = -> Fusion
  ExportMode = 0
  Group = -> [BaseFeature,Sketch,Groove,Sketch001,Groove001,Sketch002,Pocket,PolarPattern]
  Origin = -> Origin
  Tip = -> PolarPattern
  _ExportChildren = -> [BaseFeature,Groove,Groove001,Pocket,PolarPattern]
  _GroupVersion = 1
---- part krokowiec-nema17.FCStd = doc fcstd_135561158c7a ----
FCSTD DOCUMENT  (FreeCAD 2020.10.16R22739 +2665 (Git))
Label: krokowiec-nema17
License: All rights reserved
LicenseURL: http://en.wikipedia.org/wiki/All_rights_reserved
objects: Sketcher::SketchObject×5, PartDesign::Pad×3, PartDesign::Chamfer×2, PartDesign::Pocket×1, PartDesign::Hole×1, PartDesign::Body×1
note: 27 computed .brp shape members not serialized (recipe doc carries the construction recipe); baked Part::Feature solids carry a one-line shape summary decoded from their .brp

FEATURE [Sketcher::SketchObject] Sketch
  MapMode = 5
  Support = -> [XY_Plane]
  sketch-geometry (5):
    g0: LineSegment StartX=21.15 StartY=21.15 StartZ=0 EndX=-21.15 EndY=21.15 EndZ=0
    g1: LineSegment StartX=-21.15 StartY=21.15 StartZ=0 EndX=-21.15 EndY=-21.15 EndZ=0
    g2: LineSegment StartX=-21.15 StartY=-21.15 StartZ=0 EndX=21.15 EndY=-21.15 EndZ=0
    g3: LineSegment StartX=21.15 StartY=-21.15 StartZ=0 EndX=21.15 EndY=21.15 EndZ=0
    g4: Circle [constr] CenterX=0 CenterY=0 CenterZ=0 NormalX=0 NormalY=0 NormalZ=1 AngleXU=0 Radius=29.9106
  constraints (14):
    c: Coincident(g0,g1)
    c: Coincident(g1,g2)
    c: Coincident(g2,g3)
    c: Coincident(g3,g0)
    c: Equal(g0,g1)
    c: Equal(g0,g2)
    c: Equal(g0,g3)
    c: PointOnObject(g0,g4)
    c: PointOnObject(g1,g4)
    c: PointOnObject(g2,g4)
    c: PointOnObject(g3,g4)
    c: Coincident(g4,g-1)
    c: Horizontal(g0)
    c: DistanceY(g3,g3) = 42.3
FEATURE [PartDesign::Pad] Pad
  ClaimChildren = false
  Direction = (1,1,1)
  Length = 40
  Length2 = 100
  NewSolid = false
  Profile = -> Sketch
  Suppress = false
  Type = 0
FEATURE [Sketcher::SketchObject] Sketch001
  MapMode = 5
  Placement = pos=(0,0,40) rot=(0,0,1;0rad)
  Support = -> [Pad]
  sketch-geometry (1):
    g0: Circle CenterX=0 CenterY=0 CenterZ=0 NormalX=0 NormalY=0 NormalZ=1 AngleXU=0 Radius=11
  constraints (2):
    c: Coincident(g0,g-1)
    c: Diameter(g0) = 22
FEATURE [PartDesign::Pad] Pad001
  BaseFeature = -> Pad
  ClaimChildren = false
  Direction = (1,1,1)
  Length = 2
  Length2 = 100
  NewSolid = false
  Profile = -> Sketch001
  Suppress = false
  Type = 0
FEATURE [Sketcher::SketchObject] Sketch002
  MapMode = 5
  Placement = pos=(0,0,40) rot=(0,0,1;0rad)
  Support = -> [Pad001]
  sketch-geometry (1):
    g0: Circle CenterX=0 CenterY=0 CenterZ=0 NormalX=0 NormalY=0 NormalZ=1 AngleXU=0 Radius=2.5
  constraints (2):
    c: Coincident(g0,g-1)
    c: Diameter(g0) = 5
FEATURE [PartDesign::Pad] Pad002
  BaseFeature = -> Pad001
  ClaimChildren = false
  Direction = (1,1,1)
  Length = 24
  Length2 = 100
  NewSolid = false
  Profile = -> Sketch002
  Suppress = false
  Type = 0
FEATURE [PartDesign::Chamfer] Chamfer
  Angle = 45
  Base = -> Pad002 [Edge18]
  BaseFeature = -> Pad002
  ChamferType = 0
  FlipDirection = false
  NewSolid = false
  Size = 0.5
  Size2 = 1
  SupportTransform = true
  Suppress = false
FEATURE [Sketcher::SketchObject] Sketch003
  ExternalGeometry = -> [Chamfer]
  MapMode = 5
  Placement = pos=(0,0,0) rot=(1,0,0;1.5708rad)
  Support = -> [XZ_Plane]
  sketch-geometry (4):
    g0: LineSegment StartX=2 StartY=64 StartZ=0 EndX=2.5 EndY=64 EndZ=0
    g1: LineSegment StartX=2.5 StartY=64 StartZ=0 EndX=2.5 EndY=43 EndZ=0
    g2: LineSegment StartX=2.5 StartY=43 StartZ=0 EndX=2 EndY=43 EndZ=0
    g3: LineSegment StartX=2 StartY=43 StartZ=0 EndX=2 EndY=64 EndZ=0
  constraints (12):
    c: Coincident(g0,g1)
    c: Coincident(g1,g2)
    c: Coincident(g2,g3)
    c: Coincident(g3,g0)
    c: Horizontal(g0)
    c: Horizontal(g2)
    c: Vertical(g1)
    c: Vertical(g3)
    c: PointOnObject(g0,g-3)
    c: PointOnObject(g1,g-4)
    c: DistanceX(g2,g2) = 0.5
    c: DistanceY(g1,g1) = 21
FEATURE [PartDesign::Pocket] Pocket
  BaseFeature = -> Chamfer
  ClaimChildren = false
  Length = 20
  Length2 = 100
  Midplane = true
  NewSolid = false
  Profile = -> Sketch003
  Suppress = false
  Type = 1
FEATURE [Sketcher::SketchObject] Sketch004
  MapMode = 5
  Placement = pos=(0,0,40) rot=(0,0,1;0rad)
  Support = -> [Pocket]
  sketch-geometry (4):
    g0: Circle CenterX=15.5 CenterY=-15.5 CenterZ=0 NormalX=0 NormalY=0 NormalZ=1 AngleXU=0 Radius=1.25
    g1: Circle CenterX=15.5 CenterY=15.5 CenterZ=0 NormalX=0 NormalY=0 NormalZ=1 AngleXU=0 Radius=1.25
    g2: Circle CenterX=-15.5 CenterY=15.5 CenterZ=0 NormalX=0 NormalY=0 NormalZ=1 AngleXU=0 Radius=1.25
    g3: Circle CenterX=-15.5 CenterY=-15.5 CenterZ=0 NormalX=0 NormalY=0 NormalZ=1 AngleXU=0 Radius=1.25
  constraints (9):
    c: Diameter(g0) = 2.5
    c: Symmetric(g1,g0,g-1)
    c: Symmetric(g1,g2,g-2)
    c: Symmetric(g3,g2,g-1)
    c: Equal(g2,g1)
    c: Equal(g1,g3)
    c: Equal(g3,g0)
    c: DistanceX(g2,g1) = 31
    c: DistanceY(g0,g1) = 31
FEATURE [PartDesign::Hole] Hole
  BaseFeature = -> Pocket
  ClaimChildren = false
  Depth = 4
  DepthType = 0
  Diameter = 1.75
  DrillPoint = 1
  DrillPointAngle = 118
  HoleCutCountersinkAngle = 90
  HoleCutDepth = 0
  HoleCutDiameter = 1.6
  HoleCutType = 0
  ModelActualThread = false
  NewSolid = false
  Profile = -> Sketch004
  Suppress = false
  Tapered = false
  TaperedAngle = 90
  ThreadAngle = 0
  ThreadClass = 0
  ThreadCutOffInner = 0
  ThreadCutOffOuter = 0
  ThreadDirection = 0
  ThreadFit = 0
  ThreadPitch = 0
  ThreadSize = 0
  ThreadType = 1
  Threaded = false
FEATURE [PartDesign::Chamfer] Chamfer001
  Angle = 45
  Base = -> Hole [Edge26,Edge23,Edge28,Edge24]
  BaseFeature = -> Hole
  ChamferType = 0
  FlipDirection = false
  NewSolid = false
  Size = 5
  Size2 = 1
  SupportTransform = true
  Suppress = false
FEATURE [PartDesign::Body] Body  label="nema17"
  ExportMode = 0
  Group = -> [Sketch,Pad,Sketch001,Pad001,Sketch002,Pad002,Chamfer,Sketch003,Pocket,Sketch004,Hole,Chamfer001]
  Origin = -> Origin
  Tip = -> Chamfer001
  _ExportChildren = -> [Pad,Pad001,Pad002,Chamfer,Pocket,Hole,Chamfer001]
  _GroupVersion = 1
---- part m8x40imb.FCStd = doc fcstd_9782d93c9528 ----
FCSTD DOCUMENT  (FreeCAD 0.19R21911 +2545 (Git))
Label: m8x40imb
License: All rights reserved
LicenseURL: http://en.wikipedia.org/wiki/All_rights_reserved
objects: Part::Feature×1, PartDesign::FeatureBase×1, PartDesign::Body×1
note: 4 computed .brp shape members not serialized (recipe doc carries the construction recipe); baked Part::Feature solids carry a one-line shape summary decoded from their .brp

FEATURE [Part::Feature] BOLTS_part  label="Hex socket head cap screw M8 40.0"
  shape: bbox 13 x 13 x 48 mm, 13 faces (baked)
FEATURE [PartDesign::FeatureBase] BaseFeature
  BaseFeature = -> BOLTS_part
  Suppress = false
FEATURE [PartDesign::Body] Body  label="m8x40imb"
  BaseFeature = -> BOLTS_part
  ExportMode = 0
  Group = -> [BaseFeature]
  Origin = -> Origin
  Tip = -> BaseFeature
  _ExportChildren = -> [BaseFeature]
  _GroupVersion = 1
---- part plytaprzekladni.FCStd = doc fcstd_bef6aa94dc1b ----
FCSTD DOCUMENT  (FreeCAD 2020.12.13R23076 +3015 (Git))
Label: plytaprzekladni
License: All rights reserved
LicenseURL: http://en.wikipedia.org/wiki/All_rights_reserved
objects: Sketcher::SketchObject×12, PartDesign::Pocket×11, PartDesign::LinearPattern×4, PartDesign::MultiTransform×2, PartDesign::Chamfer×2, PartDesign::Pad×1, PartDesign::Fillet×1, PartDesign::Body×1
note: 70 computed .brp shape members not serialized (recipe doc carries the construction recipe); baked Part::Feature solids carry a one-line shape summary decoded from their .brp

FEATURE [Sketcher::SketchObject] Sketch
  MapMode = 5
  Support = -> [XY_Plane]
  sketch-geometry (7):
    g0: LineSegment StartX=-65 StartY=-80 StartZ=0 EndX=37 EndY=-80 EndZ=0
    g1: LineSegment StartX=37 StartY=-80 StartZ=0 EndX=37 EndY=25 EndZ=0
    g2: LineSegment StartX=37 StartY=25 StartZ=0 EndX=-65 EndY=25 EndZ=0
    g3: LineSegment StartX=-65 StartY=25 StartZ=0 EndX=-65 EndY=-80 EndZ=0
    g4: Circle CenterX=2 CenterY=0 CenterZ=0 NormalX=0 NormalY=0 NormalZ=1 AngleXU=0 Radius=11
    g5: Circle CenterX=-40 CenterY=-4e-15 CenterZ=0 NormalX=0 NormalY=0 NormalZ=1 AngleXU=0 Radius=13.5
    g6: LineSegment [constr] StartX=2 StartY=0 StartZ=0 EndX=-40 EndY=-4e-15 EndZ=0
  constraints (20):
    c: Coincident(g0,g1)
    c: Coincident(g1,g2)
    c: Coincident(g2,g3)
    c: Coincident(g3,g0)
    c: Horizontal(g0)
    c: Horizontal(g2)
    c: Vertical(g1)
    c: Vertical(g3)
    c: DistanceX(g0) = -65
    c: DistanceY(g0) = -80
    c: DistanceY(g3,g3) = 105
    c: DistanceX(g2,g2) = 102
    c: Diameter(g4) = 22
    c: Coincident(g6,g4)
    c: Coincident(g6,g5)
    c: Diameter(g5) = 27
    c: Angle(g-1,g6) = 3.14159
    c: DistanceX(g5) = -40
    c: DistanceX(g4) = 2
    c: PointOnObject(g4,g-1)
FEATURE [PartDesign::Pad] Pad
  ClaimChildren = false
  Direction = (1,1,1)
  Fit = 0
  FitJoin = 0
  InnerFit = 0
  InnerFitJoin = 0
  InnerTaperAngle = 0
  InnerTaperAngleRev = 0
  Length = 20
  Length2 = 100
  NewSolid = false
  Profile = -> Sketch
  Suppress = false
  Type = 0
FEATURE [Sketcher::SketchObject] Sketch001
  ExternalGeometry = -> [Pad]
  MapMode = 5
  Placement = pos=(0,0,20) rot=(0,0,1;0rad)
  Support = -> [Pad]
  sketch-geometry (4):
    g0: LineSegment StartX=37 StartY=-80 StartZ=0 EndX=-65 EndY=-80 EndZ=0
    g1: LineSegment StartX=-65 StartY=-80 StartZ=0 EndX=-65 EndY=-25 EndZ=0
    g2: LineSegment StartX=-65 StartY=-25 StartZ=0 EndX=37 EndY=-25 EndZ=0
    g3: LineSegment StartX=37 StartY=-25 StartZ=0 EndX=37 EndY=-80 EndZ=0
  constraints (11):
    c: Coincident(g0,g1)
    c: Coincident(g1,g2)
    c: Coincident(g2,g3)
    c: Coincident(g3,g0)
    c: Horizontal(g0)
    c: Horizontal(g2)
    c: Vertical(g1)
    c: Vertical(g3)
    c: Coincident(g0,g-3)
    c: PointOnObject(g1,g-4)
    c: DistanceY(g2) = -25
FEATURE [PartDesign::Pocket] Pocket
  BaseFeature = -> Pad
  ClaimChildren = false
  Fit = 0
  FitJoin = 0
  InnerFit = 0
  InnerFitJoin = 0
  InnerTaperAngle = 0
  InnerTaperAngleRev = 0
  Length = 10
  Length2 = 100
  NewSolid = false
  Profile = -> Sketch001
  Suppress = false
  Type = 0
FEATURE [Sketcher::SketchObject] Sketch002
  MapMode = 5
  Placement = pos=(0,0,0) rot=(1,0,0;3.14159rad)
  Support = -> [Pocket]
  sketch-geometry (5):
    g0: LineSegment StartX=23 StartY=21 StartZ=0 EndX=-19 EndY=21 EndZ=0
    g1: LineSegment StartX=-19 StartY=21 StartZ=0 EndX=-19 EndY=-21 EndZ=0
    g2: LineSegment StartX=-19 StartY=-21 StartZ=0 EndX=23 EndY=-21 EndZ=0
    g3: LineSegment StartX=23 StartY=-21 StartZ=0 EndX=23 EndY=21 EndZ=0
    g4: Circle [constr] CenterX=2 CenterY=0 CenterZ=0 NormalX=0 NormalY=0 NormalZ=1 AngleXU=0 Radius=29.6985
  constraints (15):
    c: Coincident(g0,g1)
    c: Coincident(g1,g2)
    c: Coincident(g2,g3)
    c: Coincident(g3,g0)
    c: Equal(g0,g1)
    c: Equal(g0,g2)
    c: Equal(g0,g3)
    c: PointOnObject(g0,g4)
    c: PointOnObject(g1,g4)
    c: PointOnObject(g2,g4)
    c: PointOnObject(g3,g4)
    c: Horizontal(g0)
    c: DistanceX(g0,g0) = 42
    c: PointOnObject(g4,g-1)
    c: DistanceX(g-1,g4) = 2
FEATURE [PartDesign::Pocket] Pocket001
  BaseFeature = -> Pocket
  ClaimChildren = false
  Fit = 0
  FitJoin = 0
  InnerFit = 0
  InnerFitJoin = 0
  InnerTaperAngle = 0
  InnerTaperAngleRev = 0
  Length = 16
  Length2 = 100
  NewSolid = false
  Profile = -> Sketch002
  Suppress = false
  Type = 0
FEATURE [Sketcher::SketchObject] Sketch003
  MapMode = 5
  Placement = pos=(0,0,0) rot=(1,0,0;3.14159rad)
  Support = -> [Pocket001]
  sketch-geometry (4):
    g0: ArcOfCircle CenterX=28 CenterY=35 CenterZ=0 NormalX=0 NormalY=0 NormalZ=1 AngleXU=0 Radius=2 StartAngle=3.14159 EndAngle=6.28319
    g1: ArcOfCircle CenterX=28 CenterY=45 CenterZ=0 NormalX=0 NormalY=0 NormalZ=1 AngleXU=0 Radius=2 StartAngle=0 EndAngle=3.14159
    g2: LineSegment StartX=30 StartY=35 StartZ=0 EndX=30 EndY=45 EndZ=0
    g3: LineSegment StartX=26 StartY=35 StartZ=0 EndX=26 EndY=45 EndZ=0
  constraints (10):
    c: Tangent(g0,g3) = 1.5708
    c: Tangent(g0,g2) = -1.5708
    c: Tangent(g2,g1) = -1.5708
    c: Tangent(g3,g1) = 1.5708
    c: Vertical(g2)
    c: Equal(g0,g1)
    c: Radius(g0) = 2
    c: DistanceY(g2,g2) = 10
    c: DistanceX(g0) = 28
    c: DistanceY(g0) = 35
FEATURE [PartDesign::Pocket] Pocket002
  BaseFeature = -> Pocket001
  ClaimChildren = false
  Fit = 0
  FitJoin = 0
  InnerFit = 0
  InnerFitJoin = 0
  InnerTaperAngle = 0
  InnerTaperAngleRev = 0
  Length = 5
  Length2 = 100
  NewSolid = false
  Profile = -> Sketch003
  Suppress = false
  Type = 1
FEATURE [PartDesign::LinearPattern] LinearPattern
  CopyShape = false
  Direction = -> Sketch003 [H_Axis]
  Length = 84
  NewSolid = false
  Occurrences = 4
  Reversed = true
  SubTransform = true
  Suppress = false
FEATURE [PartDesign::LinearPattern] LinearPattern001
  CopyShape = false
  Direction = -> Sketch003 [V_Axis]
  Length = 30
  NewSolid = false
  Occurrences = 2
  SubTransform = true
  Suppress = false
FEATURE [PartDesign::MultiTransform] MultiTransform
  BaseFeature = -> Pocket002
  CopyShape = false
  NewSolid = false
  OriginalSubs = -> [Pocket002]
  Originals = -> [Pocket002]
  SubTransform = true
  Suppress = false
  Transformations = -> [LinearPattern,LinearPattern001]
FEATURE [Sketcher::SketchObject] Sketch004
  MapMode = 5
  Placement = pos=(0,0,16) rot=(1,0,0;3.14159rad)
  Support = -> [MultiTransform]
  sketch-geometry (4):
    g0: Circle CenterX=16.5 CenterY=15.5 CenterZ=0 NormalX=0 NormalY=0 NormalZ=1 AngleXU=0 Radius=1.6
    g1: Circle CenterX=16.5 CenterY=-15.5 CenterZ=0 NormalX=0 NormalY=0 NormalZ=1 AngleXU=0 Radius=1.6
    g2: Circle CenterX=-14.5 CenterY=-15.5 CenterZ=0 NormalX=0 NormalY=0 NormalZ=1 AngleXU=0 Radius=1.6
    g3: Circle CenterX=-14.5 CenterY=15.5 CenterZ=0 NormalX=0 NormalY=0 NormalZ=1 AngleXU=0 Radius=1.6
  constraints (11):
    c: Equal(g0,g3)
    c: Equal(g3,g1)
    c: Equal(g1,g2)
    c: Diameter(g1) = 3.2
    c: DistanceY(g1,g0) = 31
    c: Vertical(g2,g3)
    c: Horizontal(g3,g0)
    c: Horizontal(g2,g1)
    c: DistanceX(g1) = 16.5
    c: DistanceX(g2,g1) = 31
    c: Symmetric(g0,g1,g-1)
FEATURE [PartDesign::Pocket] Pocket003
  BaseFeature = -> MultiTransform
  ClaimChildren = false
  Fit = 0
  FitJoin = 0
  InnerFit = 0
  InnerFitJoin = 0
  InnerTaperAngle = 0
  InnerTaperAngleRev = 0
  Length = 5
  Length2 = 100
  NewSolid = false
  Profile = -> Sketch004
  Suppress = false
  Type = 1
FEATURE [PartDesign::Chamfer] Chamfer
  Angle = 45
  Base = -> Pocket003 [Edge4,Edge2]
  BaseFeature = -> Pocket003
  ChamferType = 0
  FlipDirection = false
  NewSolid = false
  Size = 5
  Size2 = 1
  SupportTransform = true
  Suppress = false
FEATURE [PartDesign::Chamfer] Chamfer001
  Angle = 45
  Base = -> Chamfer [Edge91,Edge89,Edge88]
  BaseFeature = -> Chamfer
  ChamferType = 0
  FlipDirection = false
  NewSolid = false
  Size = 10
  Size2 = 1
  SupportTransform = true
  Suppress = false
FEATURE [PartDesign::Fillet] Fillet
  Base = -> Chamfer001 [Edge55]
  BaseFeature = -> Chamfer001
  NewSolid = false
  Radius = 20
  SupportTransform = true
  Suppress = false
FEATURE [Sketcher::SketchObject] Sketch006
  ExternalGeometry = -> [Fillet]
  MapMode = 5
  Placement = pos=(0,0,20) rot=(0,0,1;0rad)
  Support = -> [Fillet]
  sketch-geometry (1):
    g0: Circle CenterX=-40 CenterY=-4.25258e-11 CenterZ=0 NormalX=0 NormalY=0 NormalZ=1 AngleXU=0 Radius=16
  constraints (2):
    c: Coincident(g0,g-3)
    c: Diameter(g0) = 32
FEATURE [PartDesign::Pocket] Pocket004
  BaseFeature = -> Fillet
  ClaimChildren = false
  Fit = 0
  FitJoin = 0
  InnerFit = 0
  InnerFitJoin = 0
  InnerTaperAngle = 0
  InnerTaperAngleRev = 0
  Length = 16
  Length2 = 100
  NewSolid = false
  Profile = -> Sketch006
  Suppress = false
  Type = 0
FEATURE [Sketcher::SketchObject] Sketch007
  ExternalGeometry = -> [Pocket004]
  MapMode = 5
  Placement = pos=(0,0,20) rot=(0,0,1;0rad)
  Support = -> [Pocket004]
  sketch-geometry (4):
    g0: Circle CenterX=16.5 CenterY=15.5 CenterZ=0 NormalX=0 NormalY=0 NormalZ=1 AngleXU=0 Radius=3
    g1: Circle CenterX=-14.5 CenterY=15.5 CenterZ=0 NormalX=0 NormalY=0 NormalZ=1 AngleXU=0 Radius=3
    g2: Circle CenterX=-14.5 CenterY=-15.5 CenterZ=0 NormalX=0 NormalY=0 NormalZ=1 AngleXU=0 Radius=3
    g3: Circle CenterX=16.5 CenterY=-15.5 CenterZ=0 NormalX=0 NormalY=0 NormalZ=1 AngleXU=0 Radius=3
  constraints (8):
    c: Diameter(g3) = 6
    c: Equal(g3,g2)
    c: Equal(g3,g1)
    c: Equal(g3,g0)
    c: Coincident(g2,g-6)
    c: Coincident(g3,g-5)
    c: Coincident(g0,g-4)
    c: Coincident(g1,g-3)
FEATURE [PartDesign::Pocket] Pocket005
  BaseFeature = -> Pocket004
  ClaimChildren = false
  Fit = 0
  FitJoin = 0
  InnerFit = 0
  InnerFitJoin = 0
  InnerTaperAngle = 0
  InnerTaperAngleRev = 0
  Length = 2
  Length2 = 100
  NewSolid = false
  Profile = -> Sketch007
  Suppress = false
  Type = 0
FEATURE [Sketcher::SketchObject] Sketch008
  ExternalGeometry = -> [Pocket005]
  MapMode = 5
  Placement = pos=(0,0,16) rot=(1,0,0;3.14159rad)
  Support = -> [Pocket005]
  sketch-geometry (16):
    g0: ArcOfCircle CenterX=-14.5 CenterY=-15.5 CenterZ=0 NormalX=0 NormalY=0 NormalZ=1 AngleXU=0 Radius=1.6 StartAngle=4.71239 EndAngle=7.85398
    g1: ArcOfCircle CenterX=-16.5 CenterY=-15.5 CenterZ=0 NormalX=0 NormalY=0 NormalZ=1 AngleXU=0 Radius=1.6 StartAngle=1.5708 EndAngle=4.71239
    g2: LineSegment StartX=-14.5 StartY=-13.9 StartZ=0 EndX=-16.5 EndY=-13.9 EndZ=0
    g3: LineSegment StartX=-14.5 StartY=-17.1 StartZ=0 EndX=-16.5 EndY=-17.1 EndZ=0
    g4: ArcOfCircle CenterX=-14.5 CenterY=15.5 CenterZ=0 NormalX=0 NormalY=0 NormalZ=1 AngleXU=0 Radius=1.6 StartAngle=4.71239 EndAngle=7.85398
    g5: ArcOfCircle CenterX=-16.5 CenterY=15.5 CenterZ=0 NormalX=0 NormalY=0 NormalZ=1 AngleXU=0 Radius=1.6 StartAngle=1.5708 EndAngle=4.71239
    g6: LineSegment StartX=-14.5 StartY=17.1 StartZ=0 EndX=-16.5 EndY=17.1 EndZ=0
    g7: LineSegment StartX=-14.5 StartY=13.9 StartZ=0 EndX=-16.5 EndY=13.9 EndZ=0
    g8: ArcOfCircle CenterX=16.5 CenterY=15.5 CenterZ=0 NormalX=0 NormalY=0 NormalZ=1 AngleXU=0 Radius=1.6 StartAngle=4.71239 EndAngle=7.85398
    g9: ArcOfCircle CenterX=14.5 CenterY=15.5 CenterZ=0 NormalX=0 NormalY=0 NormalZ=1 AngleXU=0 Radius=1.6 StartAngle=1.5708 EndAngle=4.71239
    g10: LineSegment StartX=16.5 StartY=17.1 StartZ=0 EndX=14.5 EndY=17.1 EndZ=0
    g11: LineSegment StartX=16.5 StartY=13.9 StartZ=0 EndX=14.5 EndY=13.9 EndZ=0
    g12: ArcOfCircle CenterX=16.5 CenterY=-15.5 CenterZ=0 NormalX=0 NormalY=0 NormalZ=1 AngleXU=0 Radius=1.6 StartAngle=4.71239 EndAngle=7.85398
    g13: ArcOfCircle CenterX=14.5 CenterY=-15.5 CenterZ=0 NormalX=0 NormalY=0 NormalZ=1 AngleXU=0 Radius=1.6 StartAngle=1.5708 EndAngle=4.71239
    g14: LineSegment StartX=16.5 StartY=-13.9 StartZ=0 EndX=14.5 EndY=-13.9 EndZ=0
    g15: LineSegment StartX=16.5 StartY=-17.1 StartZ=0 EndX=14.5 EndY=-17.1 EndZ=0
  constraints (36):
    c: Tangent(g0,g3) = 1.5708
    c: Tangent(g0,g2) = -1.5708
    c: Tangent(g2,g1) = -1.5708
    c: Tangent(g3,g1) = 1.5708
    c: Horizontal(g2)
    c: Equal(g0,g1)
    c: Coincident(g0,g-4)
    c: Tangent(g4,g7) = 1.5708
    c: Tangent(g4,g6) = -1.5708
    c: Tangent(g6,g5) = -1.5708
    c: Tangent(g7,g5) = 1.5708
    c: Horizontal(g6)
    c: Equal(g4,g5)
    c: Coincident(g4,g-3)
    c: Tangent(g8,g11) = 1.5708
    c: Tangent(g8,g10) = -1.5708
    c: Tangent(g10,g9) = -1.5708
    c: Tangent(g11,g9) = 1.5708
    c: Horizontal(g10)
    c: Equal(g8,g9)
    c: Coincident(g8,g-6)
    c: Tangent(g12,g15) = 1.5708
    c: Tangent(g12,g14) = -1.5708
    c: Tangent(g14,g13) = -1.5708
    c: Tangent(g15,g13) = 1.5708
    c: Horizontal(g14)
    c: Equal(g12,g13)
    c: Coincident(g12,g-5)
    c: Equal(g0,g-4)
    c: Equal(g-4,g4)
    c: Equal(g4,g8)
    c: Equal(g8,g12)
    c: Equal(g6,g2)
    c: Equal(g2,g14)
    c: Equal(g14,g10)
    c: DistanceX(g14,g14) = 2
FEATURE [PartDesign::Pocket] Pocket006
  BaseFeature = -> Pocket005
  ClaimChildren = false
  Fit = 0
  FitJoin = 0
  InnerFit = 0
  InnerFitJoin = 0
  InnerTaperAngle = 0
  InnerTaperAngleRev = 0
  Length = 5
  Length2 = 100
  NewSolid = false
  Profile = -> Sketch008
  Suppress = false
  Type = 1
FEATURE [Sketcher::SketchObject] Sketch009
  ExternalGeometry = -> [Pocket006]
  MapMode = 5
  Placement = pos=(0,0,0) rot=(1,0,0;3.14159rad)
  Support = -> [Pocket006]
  sketch-geometry (4):
    g0: LineSegment StartX=-19 StartY=21 StartZ=0 EndX=-23 EndY=21 EndZ=0
    g1: LineSegment StartX=-23 StartY=21 StartZ=0 EndX=-23 EndY=-21 EndZ=0
    g2: LineSegment StartX=-23 StartY=-21 StartZ=0 EndX=-19 EndY=-21 EndZ=0
    g3: LineSegment StartX=-19 StartY=-21 StartZ=0 EndX=-19 EndY=21 EndZ=0
  constraints (10):
    c: Coincident(g0,g1)
    c: Coincident(g1,g2)
    c: Coincident(g2,g3)
    c: Coincident(g3,g0)
    c: Horizontal(g0)
    c: Horizontal(g2)
    c: Vertical(g1)
    c: Coincident(g0,g-3)
    c: Coincident(g2,g-3)
    c: DistanceX(g2,g2) = 4
FEATURE [PartDesign::Pocket] Pocket007
  BaseFeature = -> Pocket006
  ClaimChildren = false
  Fit = 0
  FitJoin = 0
  InnerFit = 0
  InnerFitJoin = 0
  InnerTaperAngle = 0
  InnerTaperAngleRev = 0
  Length = 0
  Length2 = 100
  NewSolid = false
  Profile = -> Sketch009
  Suppress = false
  Type = 3
  UpToFace = -> Pocket006 [Face52]
FEATURE [Sketcher::SketchObject] Sketch010
  ExternalGeometry = -> [Pocket007]
  MapMode = 5
  Placement = pos=(0,0,20) rot=(0,0,1;0rad)
  Support = -> [Pocket007]
  sketch-geometry (16):
    g0: ArcOfCircle CenterX=-14.5 CenterY=15.5 CenterZ=0 NormalX=0 NormalY=0 NormalZ=1 AngleXU=0 Radius=3 StartAngle=4.71239 EndAngle=7.85398
    g1: ArcOfCircle CenterX=-16.5 CenterY=15.5 CenterZ=0 NormalX=0 NormalY=0 NormalZ=1 AngleXU=0 Radius=3 StartAngle=1.5708 EndAngle=4.71239
    g2: LineSegment StartX=-14.5 StartY=18.5 StartZ=0 EndX=-16.5 EndY=18.5 EndZ=0
    g3: LineSegment StartX=-14.5 StartY=12.5 StartZ=0 EndX=-16.5 EndY=12.5 EndZ=0
    g4: ArcOfCircle CenterX=16.5 CenterY=15.5 CenterZ=0 NormalX=0 NormalY=0 NormalZ=1 AngleXU=0 Radius=3 StartAngle=4.71239 EndAngle=7.85398
    g5: ArcOfCircle CenterX=14.5 CenterY=15.5 CenterZ=0 NormalX=0 NormalY=0 NormalZ=1 AngleXU=0 Radius=3 StartAngle=1.5708 EndAngle=4.71239
    g6: LineSegment StartX=16.5 StartY=18.5 StartZ=0 EndX=14.5 EndY=18.5 EndZ=0
    g7: LineSegment StartX=16.5 StartY=12.5 StartZ=0 EndX=14.5 EndY=12.5 EndZ=0
    g8: ArcOfCircle CenterX=16.5 CenterY=-15.5 CenterZ=0 NormalX=0 NormalY=0 NormalZ=1 AngleXU=0 Radius=3 StartAngle=4.71239 EndAngle=7.85398
    g9: ArcOfCircle CenterX=14.5 CenterY=-15.5 CenterZ=0 NormalX=0 NormalY=0 NormalZ=1 AngleXU=0 Radius=3 StartAngle=1.5708 EndAngle=4.71239
    g10: LineSegment StartX=16.5 StartY=-12.5 StartZ=0 EndX=14.5 EndY=-12.5 EndZ=0
    g11: LineSegment StartX=16.5 StartY=-18.5 StartZ=0 EndX=14.5 EndY=-18.5 EndZ=0
    g12: ArcOfCircle CenterX=-14.5 CenterY=-15.5 CenterZ=0 NormalX=0 NormalY=0 NormalZ=1 AngleXU=0 Radius=3 StartAngle=4.71239 EndAngle=7.85398
    g13: ArcOfCircle CenterX=-16.5 CenterY=-15.5 CenterZ=0 NormalX=0 NormalY=0 NormalZ=1 AngleXU=0 Radius=3 StartAngle=1.5708 EndAngle=4.71239
    g14: LineSegment StartX=-14.5 StartY=-12.5 StartZ=0 EndX=-16.5 EndY=-12.5 EndZ=0
    g15: LineSegment StartX=-14.5 StartY=-18.5 StartZ=0 EndX=-16.5 EndY=-18.5 EndZ=0
  constraints (36):
    c: Tangent(g0,g3) = 1.5708
    c: Tangent(g0,g2) = -1.5708
    c: Tangent(g2,g1) = -1.5708
    c: Tangent(g3,g1) = 1.5708
    c: Horizontal(g2)
    c: Equal(g0,g1)
    c: Coincident(g0,g-3)
    c: Tangent(g4,g7) = 1.5708
    c: Tangent(g4,g6) = -1.5708
    c: Tangent(g6,g5) = -1.5708
    c: Tangent(g7,g5) = 1.5708
    c: Horizontal(g6)
    c: Equal(g4,g5)
    c: Coincident(g4,g-4)
    c: Tangent(g8,g11) = 1.5708
    c: Tangent(g8,g10) = -1.5708
    c: Tangent(g10,g9) = -1.5708
    c: Tangent(g11,g9) = 1.5708
    c: Horizontal(g10)
    c: Equal(g8,g9)
    c: Coincident(g8,g-6)
    c: Tangent(g12,g15) = 1.5708
    c: Tangent(g12,g14) = -1.5708
    c: Tangent(g14,g13) = -1.5708
    c: Tangent(g15,g13) = 1.5708
    c: Horizontal(g14)
    c: Equal(g12,g13)
    c: Coincident(g12,g-5)
    c: Equal(g12,g0)
    c: Equal(g0,g4)
    c: Equal(g4,g8)
    c: Equal(g8,g-4)
    c: Equal(g10,g14)
    c: Equal(g14,g3)
    c: Equal(g3,g7)
    c: DistanceX(g10,g10) = 2
FEATURE [PartDesign::Pocket] Pocket008
  BaseFeature = -> Pocket007
  ClaimChildren = false
  Fit = 0
  FitJoin = 0
  InnerFit = 0
  InnerFitJoin = 0
  InnerTaperAngle = 0
  InnerTaperAngleRev = 0
  Length = 0
  Length2 = 100
  NewSolid = false
  Profile = -> Sketch010
  Suppress = false
  Type = 3
  UpToFace = -> Pocket007 [Face89]
FEATURE [Sketcher::SketchObject] Sketch011
  ExternalGeometry = -> [Pocket008]
  MapMode = 5
  Placement = pos=(0,0,20) rot=(0,0,1;0rad)
  Support = -> [Pocket008]
  sketch-geometry (4):
    g0: ArcOfCircle CenterX=0 CenterY=0 CenterZ=0 NormalX=0 NormalY=0 NormalZ=1 AngleXU=0 Radius=11 StartAngle=4.71239 EndAngle=7.85398
    g1: ArcOfCircle CenterX=-2 CenterY=9e-16 CenterZ=0 NormalX=0 NormalY=0 NormalZ=1 AngleXU=0 Radius=11 StartAngle=1.5708 EndAngle=4.71239
    g2: LineSegment StartX=-5.828e-13 StartY=11 StartZ=0 EndX=-2 EndY=11 EndZ=0
    g3: LineSegment StartX=-2e-15 StartY=-11 StartZ=0 EndX=-2 EndY=-11 EndZ=0
  constraints (9):
    c: Tangent(g0,g3) = 1.5708
    c: Tangent(g0,g2) = -1.5708
    c: Tangent(g2,g1) = -1.5708
    c: Tangent(g3,g1) = 1.5708
    c: Horizontal(g2)
    c: Equal(g0,g1)
    c: Coincident(g0,g-1)
    c: Equal(g0,g-3)
    c: DistanceX(g2,g2) = 2
FEATURE [PartDesign::Pocket] Pocket009
  BaseFeature = -> Pocket008
  ClaimChildren = false
  Fit = 0
  FitJoin = 0
  InnerFit = 0
  InnerFitJoin = 0
  InnerTaperAngle = 0
  InnerTaperAngleRev = 0
  Length = 5
  Length2 = 100
  NewSolid = false
  Profile = -> Sketch011
  Suppress = false
  Type = 1
FEATURE [Sketcher::SketchObject] Sketch012
  MapMode = 5
  Placement = pos=(0,0,10) rot=(0,0,1;0rad)
  Support = -> [Pocket009]
  sketch-geometry (1):
    g0: Circle CenterX=14 CenterY=-65 CenterZ=0 NormalX=0 NormalY=0 NormalZ=1 AngleXU=0 Radius=6.5
  constraints (3):
    c: Diameter(g0) = 13
    c: DistanceX(g0) = 14
    c: DistanceY(g0) = -65
FEATURE [PartDesign::Pocket] Pocket010
  BaseFeature = -> Pocket009
  ClaimChildren = false
  Fit = 0
  FitJoin = 0
  InnerFit = 0
  InnerFitJoin = 0
  InnerTaperAngle = 0
  InnerTaperAngleRev = 0
  Length = 8
  Length2 = 100
  NewSolid = false
  Profile = -> Sketch012
  Suppress = false
  Type = 0
FEATURE [PartDesign::LinearPattern] LinearPattern002
  CopyShape = false
  Direction = -> Sketch012 [H_Axis]
  Length = 56
  NewSolid = false
  Occurrences = 3
  Reversed = true
  SubTransform = true
  Suppress = false
FEATURE [PartDesign::LinearPattern] LinearPattern003
  CopyShape = false
  Direction = -> Sketch012 [V_Axis]
  Length = 30
  NewSolid = false
  Occurrences = 3
  SubTransform = true
  Suppress = false
FEATURE [PartDesign::MultiTransform] MultiTransform001
  BaseFeature = -> Pocket010
  CopyShape = false
  NewSolid = false
  OriginalSubs = -> [Pocket010]
  Originals = -> [Pocket010]
  Refine = true
  SubTransform = true
  Suppress = false
  Transformations = -> [LinearPattern002,LinearPattern003]
FEATURE [PartDesign::Body] Body  label="plyta-przekadni"
  ExportMode = 0
  Group = -> [Sketch,Pad,Sketch001,Pocket,Sketch002,Pocket001,Sketch003,Pocket002,MultiTransform,LinearPattern,LinearPattern001,Sketch004,Pocket003,Chamfer,Chamfer001,Fillet,Sketch006,Pocket004,Sketch007,Pocket005,Sketch008,Pocket006,Sketch009,Pocket007,Sketch010,Pocket008,Sketch011,Pocket009,Sketch012,Pocket010,MultiTransform001,LinearPattern002,LinearPattern003]
  Origin = -> Origin
  Tip = -> MultiTransform001
  _ExportChildren = -> [Pad,Pocket,Pocket001,Pocket002,MultiTransform,LinearPattern,LinearPattern001,Pocket003,Chamfer,Chamfer001,Fillet,Pocket004,Pocket005,Pocket006,Pocket007,Pocket008,Pocket009,Pocket010,MultiTransform001,LinearPattern002,LinearPattern003]
  _GroupVersion = 1
---- part wkladkaloz.FCStd = doc fcstd_3d77d95a4b40 ----
FCSTD DOCUMENT  (FreeCAD 2020.12.13R23076 +3015 (Git))
Label: wkladkaloz
License: All rights reserved
LicenseURL: http://en.wikipedia.org/wiki/All_rights_reserved
objects: Sketcher::SketchObject×3, PartDesign::Pad×2, PartDesign::Chamfer×1, PartDesign::Pocket×1, PartDesign::Body×1
note: 16 computed .brp shape members not serialized (recipe doc carries the construction recipe); baked Part::Feature solids carry a one-line shape summary decoded from their .brp

FEATURE [Sketcher::SketchObject] Sketch
  MapMode = 5
  Support = -> [XY_Plane]
  sketch-geometry (1):
    g0: Circle CenterX=0 CenterY=0 CenterZ=0 NormalX=0 NormalY=0 NormalZ=1 AngleXU=0 Radius=7
  constraints (2):
    c: Coincident(g0,g-1)
    c: Diameter(g0) = 14
FEATURE [PartDesign::Pad] Pad
  ClaimChildren = false
  Direction = (1,1,1)
  Fit = 0
  FitJoin = 0
  InnerFit = 0
  InnerFitJoin = 0
  InnerTaperAngle = 0
  InnerTaperAngleRev = 0
  Length = 1
  Length2 = 100
  NewSolid = false
  Profile = -> Sketch
  Suppress = false
  Type = 0
FEATURE [Sketcher::SketchObject] Sketch001
  MapMode = 5
  Placement = pos=(0,0,1) rot=(0,0,1;0rad)
  Support = -> [Pad]
  sketch-geometry (1):
    g0: Circle CenterX=0 CenterY=0 CenterZ=0 NormalX=0 NormalY=0 NormalZ=1 AngleXU=0 Radius=6
  constraints (2):
    c: Coincident(g0,g-1)
    c: Diameter(g0) = 12
FEATURE [PartDesign::Pad] Pad001
  BaseFeature = -> Pad
  ClaimChildren = false
  Direction = (1,1,1)
  Fit = 0
  FitJoin = 0
  InnerFit = 0
  InnerFitJoin = 0
  InnerTaperAngle = 0
  InnerTaperAngleRev = 0
  Length = 15.5
  Length2 = 100
  NewSolid = false
  Profile = -> Sketch001
  Suppress = false
  Type = 0
FEATURE [PartDesign::Chamfer] Chamfer
  Angle = 45
  Base = -> Pad001 [Edge6]
  BaseFeature = -> Pad001
  ChamferType = 0
  FlipDirection = false
  NewSolid = false
  Size = 1
  Size2 = 1
  SupportTransform = true
  Suppress = false
FEATURE [Sketcher::SketchObject] Sketch002
  MapMode = 5
  Placement = pos=(0,0,16.5) rot=(0,0,1;0rad)
  Support = -> [Chamfer]
  sketch-geometry (1):
    g0: Circle CenterX=0 CenterY=0 CenterZ=0 NormalX=0 NormalY=0 NormalZ=1 AngleXU=0 Radius=3.85
  constraints (3):
    c: PointOnObject(g0,g-2)
    c: Diameter(g0) = 7.7
    c: DistanceY(g0) = 0
FEATURE [PartDesign::Pocket] Pocket
  BaseFeature = -> Chamfer
  ClaimChildren = false
  Fit = 0
  FitJoin = 0
  InnerFit = 0
  InnerFitJoin = 0
  InnerTaperAngle = 0
  InnerTaperAngleRev = 0
  Length = 5
  Length2 = 100
  NewSolid = false
  Profile = -> Sketch002
  Suppress = false
  Type = 1
FEATURE [PartDesign::Body] Body  label="wkladkamimosr"
  ExportMode = 0
  Group = -> [Sketch,Pad,Sketch001,Pad001,Chamfer,Sketch002,Pocket]
  Origin = -> Origin
  Tip = -> Pocket
  _ExportChildren = -> [Pad,Pad001,Chamfer,Pocket]
  _GroupVersion = 1
